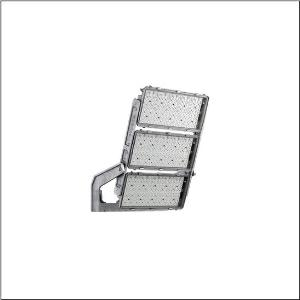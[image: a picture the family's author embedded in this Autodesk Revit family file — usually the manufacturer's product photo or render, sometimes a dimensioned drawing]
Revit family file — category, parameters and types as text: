
# Revit family: floodlight_fl_11_maxi_pro_remote___pl52_5xa779426d01ba_5366
name_source: partatom
category: Lighting Fixtures
units: mm (PartAtom-declared; Revit-internal decimal feet)

## family parameters
Cut with Voids When Loaded = No
Host = Face
Light Source = No
Part Type = Normal
Room Calculation Point = No
Round Connector Dimension = Use Diameter
Shared = No

## types (1)
- --- (1 x LED, 146220 lm, 1095.8 W, 4000K)
    Apparent Load = 1096 VA
    CIE Flux Codes = 24 55 98 100 100
    Color Rendering = 70
    Color Temperature = 4000K
    Default Elevation = 1800 mm
    Description = Floodlight FL 11  maxi  pro Remote floodlight; light control with lens of PMMA; cover panel of toughened safety glass, transparent; light distribution: PL52, asymmetric direct distribution, LEDcolour temperature: 4000K, rated luminous flux: 146.220lm, colour rendering: CRI > 70, light colour: 740; luminous efficacy: 133lm/W; brightness control: DALI 2 (1 DALI address); with terminal, 8-pole, max. 2.5mm², mains connection: 220..240V/380..400V AC, 50/60Hz, surge voltage resistance: line to ground: 10kV, ECG replaceable separately, LED unit replaceable without ESD environment, dustproof LED module, dimming range 10..100%, no afterglow with DALI off / DMX off command; 1096W floodlight with 3x LED unit of diecast aluminium, coated grey; length: 713mm / width: 651mm / height: 338mm; mounting bracket, of diecast aluminium, uncoated, natural, equipment: Longlife, protection rating (complete): IP66; insulation class (complete): insulation class I (protective earthing); certification: CE, ENEC, VDE; ball protection: ball impact resistance with accessories, impact resistance: IK07; rated ambient temperature 10°C, only for outdoor installations, permissible operating ambient temperature: -40..+40°C, permissible storage temperature: -40..+85°C; packaging unit: 1 piece

Light Distribution: PL52
    Height = 320 mm
    Lamp = 1 x LED
    Lamp Light Flux = 146220 lm
    Lamp Power = 1095.8 W
    Lamp count = 1
    Length = 1002 mm
    Luminous efficacy = 133 lm/W
    Manufacturer = Siteco
    ModVariant = No
    Model = 5XA779426D01BA
    Mounting Place = Ceiling
    Mounting Type = Surface mounted
    Number of Poles = 1
    OnlyDefault = Yes
    Power Factor = 1
    Product Name = Floodlight FL 11 maxi pro Remote | PL52
    Product group = floodlight | ceiling mounted
    ProductGroupID = 303
    Protection Class = Protection class I
    Protection Degree = IP 66
    RLX_Detail_Level = 1
    RLX_Emergency_Light_Flux = 0 lm
    RLX_Emergency_Type = 0
    RLX_Emergency_Type_DB = No
    RlxData = <blob elided: 52605 chars, md5=82aec002>
    Socket = socket
    Standby Power = 0 W
    System Light Flux = 146220 lm
    System Power = 1096 W
    Type Comments = factory setting: luminous flux: 100 % | dim-lin: 254 | 760 mA
    Type Image = l_1006784.jpg
    URL = http://relux.com
    VarID = @adj_046307
    Voltage = 0 V
    Weight = 0.00 kg
    Width = 655 mm

## geometry (parser evidence)
native form markers: Blend x4, Sweep x13
no freeform markers — native parametric forms only
